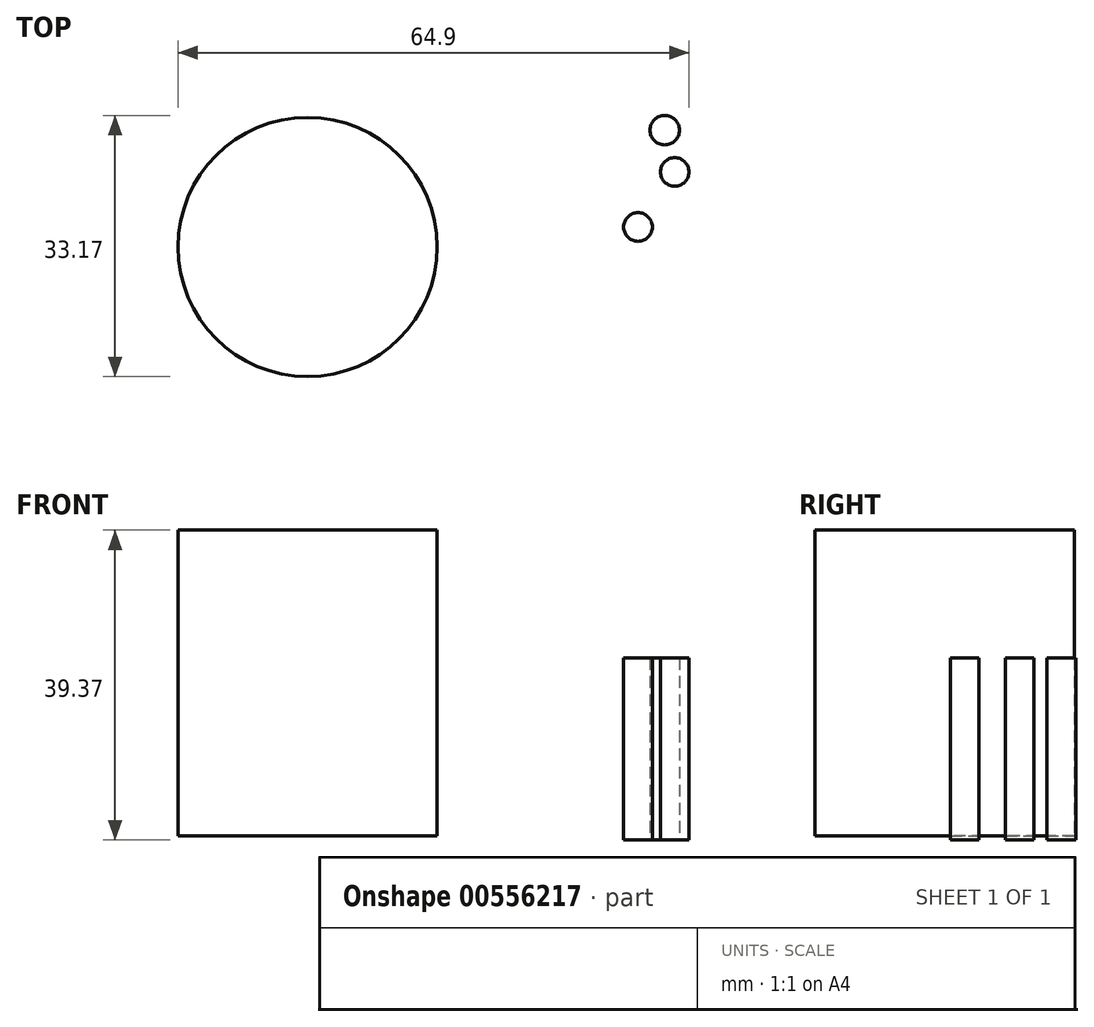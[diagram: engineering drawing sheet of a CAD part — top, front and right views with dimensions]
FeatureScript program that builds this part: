
annotation { "Feature Type Name" : "Feature", "Feature Type Description" : "" }
export const myFeature = defineFeature(function(context is Context, id is Id, definition is map)
    precondition{}
    {
        {
            var Q0;
            Q0=qCreatedBy(makeId("Top.planeOp"),FACE);
            var sketch = newSketch(context, id + "F0", { "sketchPlane" : qUnion([Q0])});
            skCircle(sketch, "E0", {"center": v(-25.43, 29.35) * mm, "radius": 16.46 * mm});
            skSolve(sketch);
        }
        {
            var Q0;
            Q0 = qSketchRegion(id + "F0", true);
            extrude(context, id + "F1", {"entities" : qUnion([Q0]), "depth" : 39.37 * mm, "offsetDistance" : 25.4 * mm});
        }
        {
            var Q0;
            Q0=makeQuery(id+"F1.opExtrude","CAP_FACE",FACE,{"disambiguationData":[OSD([sQuery(id+"F0.wireOp",EDGE,"E0")])],"isStart":true});
            extrude(context, id + "F2", {"entities" : qUnion([Q0]), "operationType" : NewBodyOperationType.REMOVE, "oppositeDirection" : true, "depth" : 0.5 * mm, "offsetDistance" : 25.4 * mm});
        }
        {
            var Q0;
            Q0=qCreatedBy(makeId("Top.planeOp"),FACE);
            var sketch = newSketch(context, id + "F3", { "sketchPlane" : qUnion([Q0])});
            skCircle(sketch, "E1", {"center": v(19.92, 44.2) * mm, "radius": 1.87 * mm});
            skCircle(sketch, "E2", {"center": v(16.53, 31.9) * mm, "radius": 1.82 * mm});
            skCircle(sketch, "E3", {"center": v(21.2, 38.9) * mm, "radius": 1.81 * mm});
            skSolve(sketch);
        }
        {
            var Q0;
            Q0=makeQuery(id+"F3.imprint","IMPRINT",FACE,{"disambiguationData":[TD([[makeQuery(id+"F3.imprint","IMPRINT",EDGE,{"derivedFrom":sQuery(id+"F3.wireOp",EDGE,"E2")}),1.0]])]});
            var Q1;
            Q1=makeQuery(id+"F3.imprint","IMPRINT",FACE,{"disambiguationData":[TD([[makeQuery(id+"F3.imprint","IMPRINT",EDGE,{"derivedFrom":sQuery(id+"F3.wireOp",EDGE,"E3")}),1.0]])]});
            var Q2;
            Q2=makeQuery(id+"F3.imprint","IMPRINT",FACE,{"disambiguationData":[TD([[makeQuery(id+"F3.imprint","IMPRINT",EDGE,{"derivedFrom":sQuery(id+"F3.wireOp",EDGE,"E1")}),1.0]])]});
            extrude(context, id + "F4", {"entities" : qUnion([Q0, Q1, Q2]), "depth" : 23.1 * mm, "offsetDistance" : 25.4 * mm});
        }
    });
